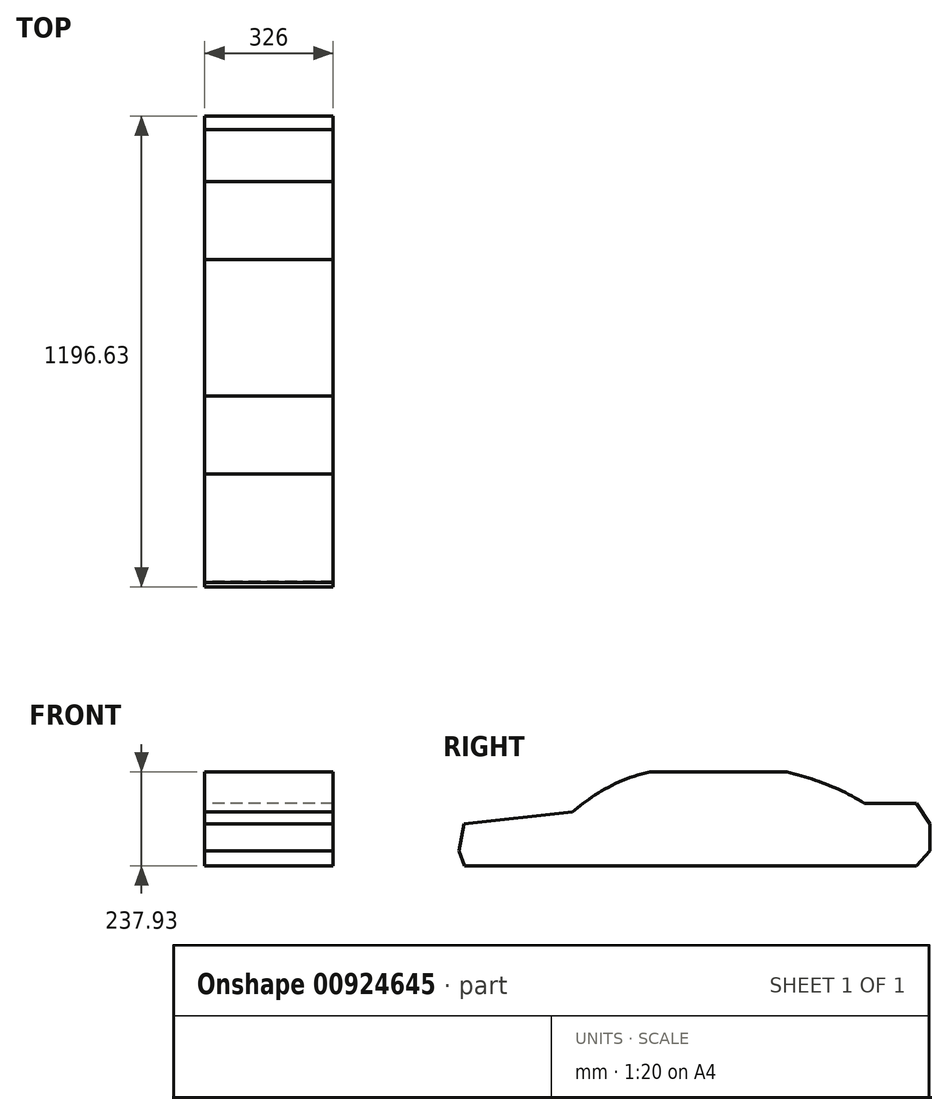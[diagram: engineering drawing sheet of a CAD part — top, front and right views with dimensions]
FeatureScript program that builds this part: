
annotation { "Feature Type Name" : "Feature", "Feature Type Description" : "" }
export const myFeature = defineFeature(function(context is Context, id is Id, definition is map)
    precondition{}
    {
        {
            var Q0;
            Q0=qCreatedBy(makeId("Right.planeOp"),FACE);
            var sketch = newSketch(context, id + "F0", { "sketchPlane" : qUnion([Q0])});
            skLineSegment(sketch, "E0", {"start": v(-352.31, 87.54) * mm, "end": v(-76.61, 118.1) * mm});
            skLineSegment(sketch, "E1", {"start": v(120.46, 219.22) * mm, "end": v(468.1, 219.22) * mm});
            skLineSegment(sketch, "E2", {"start": v(-352.31, 87.54) * mm, "end": v(-364.6, 19.2) * mm});
            skLineSegment(sketch, "E3", {"start": v(-364.6, 19.2) * mm, "end": v(-350.53, -18.71) * mm});
            skLineSegment(sketch, "E4", {"start": v(-350.53, -18.71) * mm, "end": v(798.05, -18.71) * mm});
            skLineSegment(sketch, "E5", {"start": v(798.05, -18.71) * mm, "end": v(832.03, 19.2) * mm});
            skLineSegment(sketch, "E6", {"start": v(832.03, 19.2) * mm, "end": v(832.03, 87.54) * mm});
            skLineSegment(sketch, "E7", {"start": v(832.03, 87.54) * mm, "end": v(798.05, 140.19) * mm});
            skLineSegment(sketch, "E8", {"start": v(798.05, 140.19) * mm, "end": v(665.27, 140.19) * mm});
            skFitSpline(sketch, "E9", {"points": [v(-76.61, 118.1) * mm, v(120.46, 219.22) * mm], "startDerivative": vector(150.4, 123.49) * mm, "endDerivative": vector(241.45, 44.45) * mm});
            skFitSpline(sketch, "E10", {"points": [v(468.1, 219.22) * mm, v(665.27, 140.19) * mm], "startDerivative": vector(220.41, -51.97) * mm, "endDerivative": vector(183.02, -113.64) * mm});
            skSolve(sketch);
        }
        {
            var Q0;
            Q0=makeQuery(id+"F0.imprint","IMPRINT",FACE,{"disambiguationData":[TD([[makeQuery(id+"F0.imprint","IMPRINT",EDGE,{"derivedFrom":sQuery(id+"F0.wireOp",EDGE,"E0")}),-1.0]])]});
            extrude(context, id + "F1", {"entities" : qUnion([Q0]), "depth" : 326 * mm, "offsetDistance" : 25 * mm});
        }
    });
